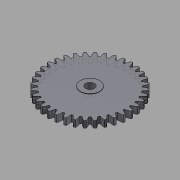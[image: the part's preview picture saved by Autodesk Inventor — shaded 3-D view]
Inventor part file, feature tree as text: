
AUTODESK INVENTOR PART (.ipt)
format: ipt  version: 2015 (Build 190159000, 159)  size: 326,144 bytes
history: native  units: in
note: dims shown in document units (in); Inventor stores cm internally (conversion verified against a paired STEP export)
features: other x13, sketch x4, plane x2
ambient origin geometry x8: Origin, YZ Plane, XZ Plane, XY Plane, X Axis, Y Axis, Z Axis, Center Point
bodies: Solid1 (feature_tree)
feature tree (19):
  other  "Spur Gear27_MIR1.ipt"
  other  "Solid1::Spur Gear27_MIR1.ipt"
  other  "TaggingFeature1"
  sketch  "Sketch1"  dims[d0=0.3937in]
  sketch  "Sketch2"  dims[d16=0.4528in d17=0.0in d41=0.0in d43=0.4528in d46=0.4528in d47=0.0in d48=0.0in]
  sketch  "Sketch3"
  sketch  "Sketch4"
  plane  "XZ Plane_1"
  plane  "Work Plane2"
  other  "Z Axis_1"
  other  "Srf1"
  other  "Srf1::Derived"
  other  "Distance iMate"
  other  "Align iMate"
  other  "Mesh iMate"
  other  "Axis iMate"
  other  "Position iMate"
  other  "Mesh iMate2"
  other  "Start plane iMate"
